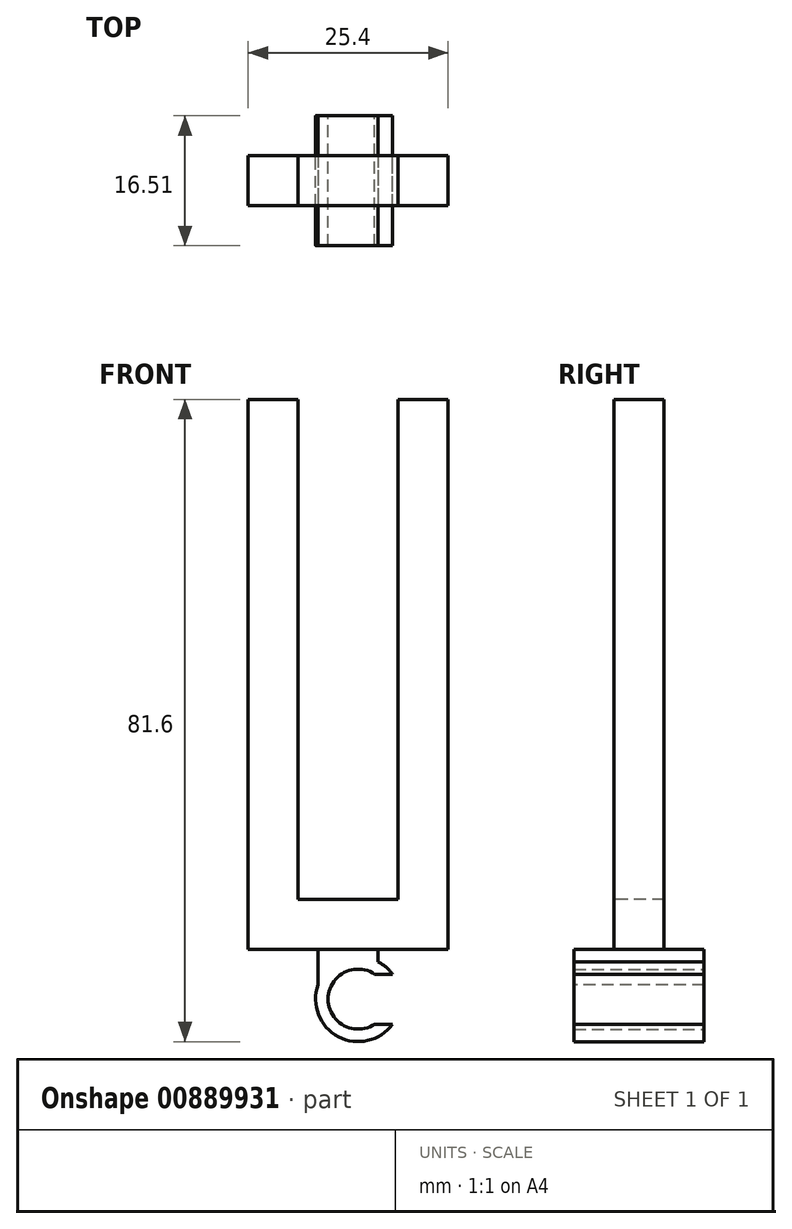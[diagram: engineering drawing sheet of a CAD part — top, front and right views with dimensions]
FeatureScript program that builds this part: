
annotation { "Feature Type Name" : "Feature", "Feature Type Description" : "" }
export const myFeature = defineFeature(function(context is Context, id is Id, definition is map)
    precondition{}
    {
        {
            var Q0;
            Q0=qCreatedBy(makeId("Front.planeOp"),FACE);
            var sketch = newSketch(context, id + "F0", { "sketchPlane" : qUnion([Q0])});
            skArc(sketch, "E0", {"start": v(2.1, 3.18) * mm, "mid": v(-3.81, 0) * mm, "end": v(2.1, -3.18) * mm});
            skArc(sketch, "E1.0", {"start": v(4.36, 3.18) * mm, "mid": v(-5.4, 0) * mm, "end": v(4.36, -3.18) * mm});
            skLineSegment(sketch, "E2", {"start": v(-5.4, 0) * mm, "end": v(5.4, 0) * mm, "construction": true});
            skLineSegment(sketch, "E3", {"start": v(-6.63, 3.18) * mm, "end": v(7.37, 3.18) * mm, "construction": true});
            skLineSegment(sketch, "E4", {"start": v(-6.34, -3.18) * mm, "end": v(7.33, -3.18) * mm, "construction": true});
            skLineSegment(sketch, "E5", {"start": v(2.1, 3.18) * mm, "end": v(4.36, 3.18) * mm});
            skLineSegment(sketch, "E6", {"start": v(2.1, -3.18) * mm, "end": v(4.36, -3.18) * mm});
            skPoint(sketch, "E6.startSnap0", {"position": v(0.5, -3.18) * mm});
            skSolve(sketch);
        }
        {
            var Q0;
            Q0=qSketchRegion(id+"F0",true);
            extrude(context, id + "F1", {"entities" : qUnion([Q0]), "depth" : 73.66 * mm, "offsetDistance" : 25.4 * mm});
        }
        {
            var Q0;
            Q0=makeQuery(id+"F1.opExtrude","CAP_FACE",FACE,{"disambiguationData":[OSD([sQuery(id+"F0.wireOp",EDGE,"E0"),sQuery(id+"F0.wireOp",EDGE,"E1.0"),sQuery(id+"F0.wireOp",EDGE,"E5"),sQuery(id+"F0.wireOp",EDGE,"E6")])],"isStart":false});
            var sketch = newSketch(context, id + "F2", { "sketchPlane" : qUnion([Q0])});
            skLineSegment(sketch, "E7", {"start": v(-5.08, 1.82) * mm, "end": v(-5.08, 6.35) * mm});
            skLineSegment(sketch, "E8", {"start": v(2.54, 4.76) * mm, "end": v(2.54, 6.35) * mm});
            skLineSegment(sketch, "E9", {"start": v(2.54, 6.35) * mm, "end": v(-5.08, 6.35) * mm});
            skArc(sketch, "E10.0", {"start": v(2.54, 4.76) * mm, "mid": v(-1.94, 5.04) * mm, "end": v(-5.08, 1.82) * mm});
            skPoint(sketch, "E11.orphan", {"position": v(4.36, -3.18) * mm});
            skPoint(sketch, "E12.orphan", {"position": v(4.36, 3.18) * mm});
            skSolve(sketch);
        }
        {
            var Q0;
            Q0=qSketchRegion(id+"F2",true);
            var Q1;
            Q1=makeQuery(id+"F1.opExtrude","CAP_FACE",FACE,{"disambiguationData":[OSD([sQuery(id+"F0.wireOp",EDGE,"E0"),sQuery(id+"F0.wireOp",EDGE,"E1.0"),sQuery(id+"F0.wireOp",EDGE,"E5"),sQuery(id+"F0.wireOp",EDGE,"E6")])],"isStart":true});
            extrude(context, id + "F3", {"entities" : qUnion([Q0]), "operationType" : NewBodyOperationType.ADD, "endBound" : BoundingType.UP_TO_SURFACE, "oppositeDirection" : true, "depth" : 25.4 * mm, "endBoundEntityFace" : qUnion([Q1]), "offsetDistance" : 25.4 * mm});
        }
        {
            var Q0;
            Q0=makeQuery(id+"F3.opExtrude","SWEPT_FACE",FACE,{"disambiguationData":[OSD([sQuery(id+"F2.wireOp",EDGE,"E9")])]});
            var sketch = newSketch(context, id + "F4", { "sketchPlane" : qUnion([Q0])});
            skLineSegment(sketch, "E13", {"start": v(-5.08, -36.83) * mm, "end": v(2.54, -36.83) * mm, "construction": true});
            skLineSegment(sketch, "E14", {"start": v(-13.97, -68.58) * mm, "end": v(11.43, -68.58) * mm});
            skLineSegment(sketch, "E15", {"start": v(-1.27, -73.66) * mm, "end": v(-1.27, 0) * mm, "construction": true});
            skLineSegment(sketch, "E16", {"start": v(-13.97, -68.58) * mm, "end": v(-13.97, -5.08) * mm, "construction": true});
            skLineSegment(sketch, "E17", {"start": v(-13.97, -5.08) * mm, "end": v(11.43, -5.08) * mm});
            skLineSegment(sketch, "E18", {"start": v(11.43, -5.08) * mm, "end": v(11.43, -68.58) * mm, "construction": true});
            skLineSegment(sketch, "E19.0", {"start": v(-13.97, -11.43) * mm, "end": v(11.43, -11.43) * mm});
            skLineSegment(sketch, "E20", {"start": v(-13.97, -5.08) * mm, "end": v(-13.97, -11.43) * mm});
            skLineSegment(sketch, "E21", {"start": v(11.43, -5.08) * mm, "end": v(11.43, -11.43) * mm});
            skLineSegment(sketch, "E22.0", {"start": v(-13.97, -62.23) * mm, "end": v(11.43, -62.23) * mm});
            skLineSegment(sketch, "E23", {"start": v(11.43, -62.23) * mm, "end": v(11.43, -68.58) * mm});
            skLineSegment(sketch, "E24", {"start": v(-13.97, -62.23) * mm, "end": v(-13.97, -68.58) * mm});
            skSolve(sketch);
        }
        {
            var Q0;
            Q0=qSketchRegion(id+"F4",true);
            extrude(context, id + "F5", {"entities" : qUnion([Q0]), "operationType" : NewBodyOperationType.ADD, "depth" : 69.85 * mm, "offsetDistance" : 25.4 * mm});
        }
        {
            var Q0;
            Q0=makeQuery(id+"F5.opExtrude","SWEPT_FACE",FACE,{"disambiguationData":[OSD([sQuery(id+"F4.wireOp",EDGE,"E14")])]});
            var sketch = newSketch(context, id + "F6", { "sketchPlane" : qUnion([Q0])});
            skLineSegment(sketch, "E25", {"start": v(-1.27, 76.2) * mm, "end": v(-1.27, -11.05) * mm, "construction": true});
            skLineSegment(sketch, "E26.0", {"start": v(-7.62, 76.2) * mm, "end": v(-7.62, 12.7) * mm});
            skLineSegment(sketch, "E27.0", {"start": v(5.08, 76.2) * mm, "end": v(5.08, 12.7) * mm});
            skLineSegment(sketch, "E28", {"start": v(-7.62, 12.7) * mm, "end": v(5.08, 12.7) * mm});
            skLineSegment(sketch, "E29", {"start": v(-7.62, 76.2) * mm, "end": v(5.08, 76.2) * mm});
            skSolve(sketch);
        }
        {
            var Q0;
            Q0=qSketchRegion(id+"F6",true);
            var Q1;
            Q1=makeQuery(id+"F5.opExtrude","SWEPT_FACE",FACE,{"disambiguationData":[OSD([sQuery(id+"F4.wireOp",EDGE,"E17")])]});
            extrude(context, id + "F7", {"entities" : qUnion([Q0]), "operationType" : NewBodyOperationType.REMOVE, "endBound" : BoundingType.UP_TO_SURFACE, "oppositeDirection" : true, "depth" : 25.4 * mm, "endBoundEntityFace" : qUnion([Q1]), "offsetDistance" : 25.4 * mm});
        }
        {
            var Q0;
            Q0=makeQuery(id+"F3.boolean.opBoolean","MERGE",FACE,{"derivedFrom":[makeQuery(id+"F1.opExtrude","CAP_FACE",FACE,{"disambiguationData":[OSD([sQuery(id+"F0.wireOp",EDGE,"E0"),sQuery(id+"F0.wireOp",EDGE,"E1.0"),sQuery(id+"F0.wireOp",EDGE,"E5"),sQuery(id+"F0.wireOp",EDGE,"E6")])],"isStart":true}),makeQuery(id+"F3.opExtrude","CAP_FACE",FACE,{"disambiguationData":[OSD([sQuery(id+"F2.wireOp",EDGE,"E7"),sQuery(id+"F2.wireOp",EDGE,"E8"),sQuery(id+"F2.wireOp",EDGE,"E9"),sQuery(id+"F2.wireOp",EDGE,"E10.0")])],"isStart":false})]});
            var sketch = newSketch(context, id + "F8", { "sketchPlane" : qUnion([Q0])});
            skLineSegment(sketch, "E30.0", {"start": v(-11.43, 76.2) * mm, "end": v(-11.43, 6.35) * mm, "construction": true});
            skLineSegment(sketch, "E31", {"start": v(-11.43, 76.2) * mm, "end": v(-11.43, -6.35) * mm});
            skLineSegment(sketch, "E32", {"start": v(-11.43, -6.35) * mm, "end": v(13.97, -6.35) * mm});
            skLineSegment(sketch, "E33", {"start": v(13.97, 76.2) * mm, "end": v(13.97, -6.35) * mm});
            skLineSegment(sketch, "E34", {"start": v(-11.43, 76.2) * mm, "end": v(13.97, 76.2) * mm});
            skSolve(sketch);
        }
        {
            var Q0;
            Q0 = qSketchRegion(id + "F8", true);
            extrude(context, id + "F9", {"entities" : qUnion([Q0]), "operationType" : NewBodyOperationType.REMOVE, "oppositeDirection" : true, "depth" : 57.15 * mm, "offsetDistance" : 25.4 * mm});
        }
    });
